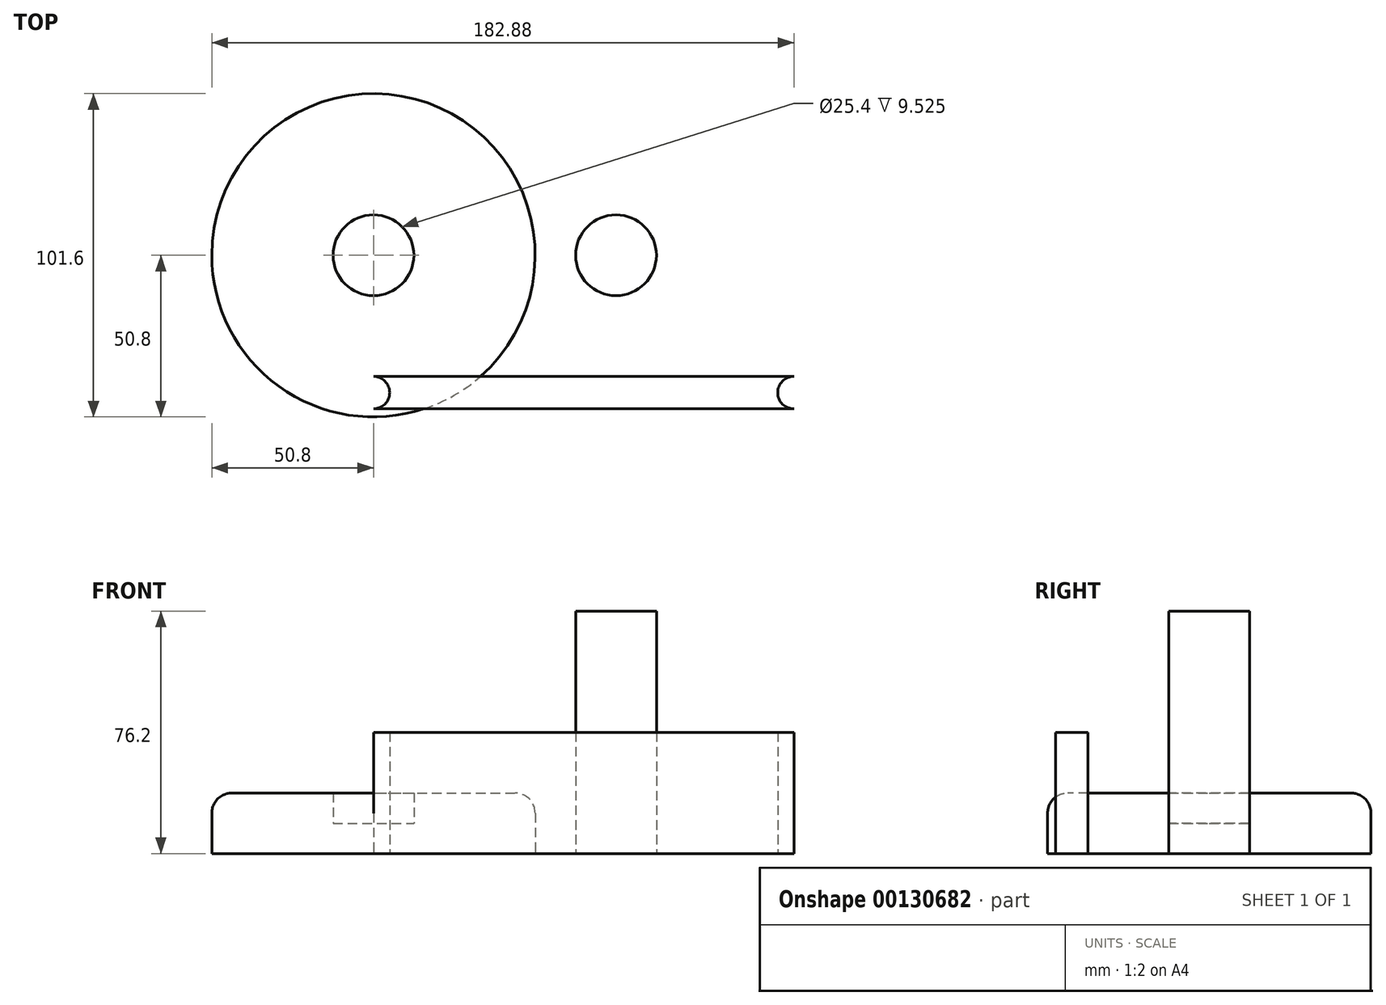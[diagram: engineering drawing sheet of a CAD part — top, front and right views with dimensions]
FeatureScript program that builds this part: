
annotation { "Feature Type Name" : "Feature", "Feature Type Description" : "" }
export const myFeature = defineFeature(function(context is Context, id is Id, definition is map)
    precondition{}
    {
        {
            var Q0;
            Q0=qCreatedBy(makeId("Top.planeOp"),FACE);
            var sketch = newSketch(context, id + "F0", { "sketchPlane" : qUnion([Q0])});
            skCircle(sketch, "E0", {"center": v(0, 0) * mm, "radius": 12.7 * mm});
            skLineSegment(sketch, "E1.bottom", {"start": v(0, -48.26) * mm, "end": v(132.08, -48.26) * mm});
            skLineSegment(sketch, "E1.top", {"start": v(0, -38.1) * mm, "end": v(132.08, -38.1) * mm});
            skLineSegment(sketch, "E1.left", {"start": v(0, -48.26) * mm, "end": v(0, -38.1) * mm});
            skLineSegment(sketch, "E1.right", {"start": v(132.08, -48.26) * mm, "end": v(132.08, -38.1) * mm});
            skCircle(sketch, "E2", {"center": v(0, -43.18) * mm, "radius": 5.08 * mm});
            skCircle(sketch, "E3", {"center": v(132.08, -43.18) * mm, "radius": 5.08 * mm});
            skSolve(sketch);
        }
        {
            var Q0;
            Q0=makeQuery(id+"F0.imprint","IMPRINT",FACE,{"disambiguationData":[TD([[makeQuery(id+"F0.imprint","IMPRINT",EDGE,{"derivedFrom":sQuery(id+"F0.wireOp",EDGE,"E0")}),1.0]])]});
            extrude(context, id + "F1", {"entities" : qUnion([Q0]), "depth" : 76.2 * mm});
        }
        {
            var Q0;
            Q0=makeQuery(id+"F1.opExtrude","SWEPT_BODY",BODY,{"disambiguationData":[OSD([sQuery(id+"F0.wireOp",EDGE,"E0")])]});
            transform(context, id + "F2", {"entities" : qUnion([Q0]), "transformType" : TransformType.TRANSLATION_3D, "dx" : 76.2 * mm, "dy" : 0 * mm, "dz" : 0 * mm, "makeCopy" : false});
        }
        {
            var Q0;
            Q0=qCreatedBy(makeId("Front.planeOp"),FACE);
            var sketch = newSketch(context, id + "F3", { "sketchPlane" : qUnion([Q0])});
            skLineSegment(sketch, "E4.bottom", {"start": v(0, 0) * mm, "end": v(-50.8, 0) * mm});
            skLineSegment(sketch, "E4.top", {"start": v(0, 19.05) * mm, "end": v(-44.45, 19.05) * mm});
            skLineSegment(sketch, "E4.left", {"start": v(0, 0) * mm, "end": v(0, 19.05) * mm});
            skLineSegment(sketch, "E4.right", {"start": v(-50.8, 0) * mm, "end": v(-50.8, 12.7) * mm});
            skLineSegment(sketch, "E5.bottom", {"start": v(0, 19.05) * mm, "end": v(-12.7, 19.05) * mm});
            skLineSegment(sketch, "E5.top", {"start": v(0, 9.52) * mm, "end": v(-12.7, 9.52) * mm});
            skLineSegment(sketch, "E5.left", {"start": v(0, 19.05) * mm, "end": v(0, 9.52) * mm});
            skLineSegment(sketch, "E5.right", {"start": v(-12.7, 19.05) * mm, "end": v(-12.7, 9.52) * mm});
            skPoint(sketch, "E6.visualSharp", {"position": v(-50.8, 19.05) * mm});
            skArc(sketch, "E6.filletArc", {"start": v(-44.45, 19.05) * mm, "mid": v(-48.94, 17.2) * mm, "end": v(-50.8, 12.7) * mm});
            skSolve(sketch);
        }
        {
            var Q0;
            {var subQ1=sQuery(id+"F3.wireOp",EDGE,"E4.bottom");Q0=makeQuery(id+"F3.imprint","IMPRINT",FACE,{"disambiguationData":[TD([[makeQuery(id+"F3.imprint","IMPRINT",EDGE,{"derivedFrom":subQ1}),-1.0]])]});}
            var Q1;
            Q1=sQuery(id+"F3.wireOp",EDGE,"E4.left");
            revolve(context, id + "F4", {"entities" : qUnion([Q0]), "axis" : qUnion([Q1]), "revolveType" : RevolveType.FULL});
        }
        {
            var Q0;
            {var subQ0=sQuery(id+"F0.wireOp",EDGE,"E1.bottom");Q0=makeQuery(id+"F0.imprint","IMPRINT",FACE,{"disambiguationData":[TD([[makeQuery(id+"F0.imprint","IMPRINT",EDGE,{"derivedFrom":subQ0}),1.0]])]});}
            extrude(context, id + "F5", {"entities" : qUnion([Q0]), "depth" : 38.1 * mm});
        }
    });
